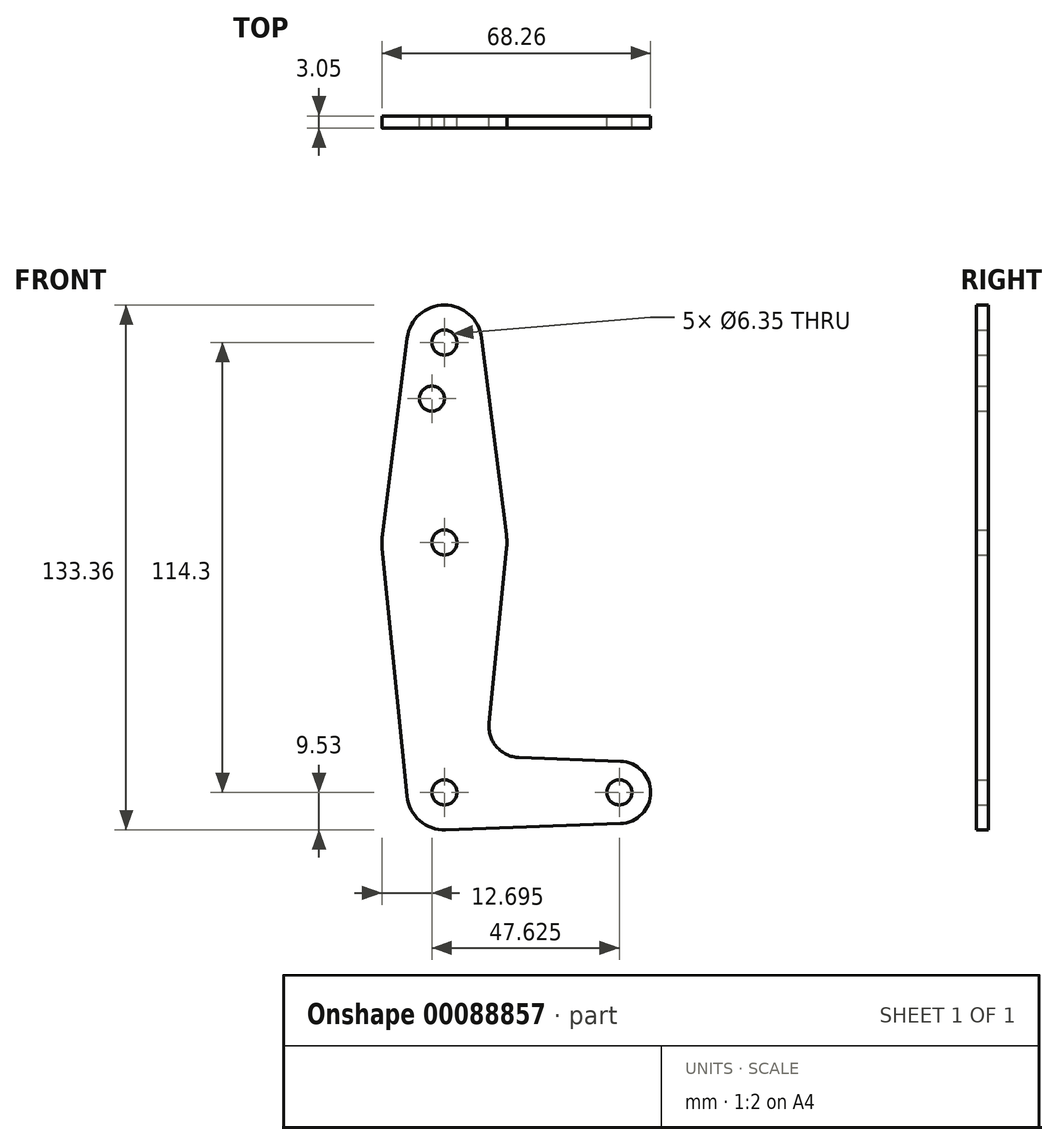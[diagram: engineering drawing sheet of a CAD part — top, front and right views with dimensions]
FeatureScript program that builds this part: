
annotation { "Feature Type Name" : "Feature", "Feature Type Description" : "" }
export const myFeature = defineFeature(function(context is Context, id is Id, definition is map)
    precondition{}
    {
        {
            var Q0;
            Q0=qCreatedBy(makeId("Front.planeOp"),FACE);
            var sketch = newSketch(context, id + "F0", { "sketchPlane" : qUnion([Q0])});
            skCircle(sketch, "E0", {"center": v(0, 114.3) * mm, "radius": 9.53 * mm});
            skCircle(sketch, "E1", {"center": v(0, 63.5) * mm, "radius": 15.88 * mm});
            skCircle(sketch, "E2", {"center": v(0, 0) * mm, "radius": 9.53 * mm});
            skCircle(sketch, "E3", {"center": v(44.45, 0) * mm, "radius": 7.94 * mm});
            skLineSegment(sketch, "E4", {"start": v(0, 0) * mm, "end": v(44.45, 0) * mm, "construction": true});
            skLineSegment(sketch, "E5", {"start": v(0, 114.3) * mm, "end": v(0, 0) * mm, "construction": true});
            skLineSegment(sketch, "E6", {"start": v(0.34, -9.52) * mm, "end": v(44.73, -7.93) * mm});
            skLineSegment(sketch, "E7", {"start": v(18.97, 8.85) * mm, "end": v(44.73, 7.93) * mm});
            skCircle(sketch, "E8", {"center": v(0, 114.3) * mm, "radius": 3.18 * mm});
            skLineSegment(sketch, "E9", {"start": v(-9.45, 115.5) * mm, "end": v(-15.75, 65.48) * mm});
            skLineSegment(sketch, "E10", {"start": v(-15.8, 61.91) * mm, "end": v(-9.48, -0.95) * mm});
            skLineSegment(sketch, "E11", {"start": v(9.45, 115.5) * mm, "end": v(15.75, 65.48) * mm});
            skLineSegment(sketch, "E12", {"start": v(15.8, 61.91) * mm, "end": v(11.34, 17.6) * mm});
            skCircle(sketch, "E13", {"center": v(0, 0) * mm, "radius": 3.18 * mm});
            skCircle(sketch, "E14", {"center": v(44.45, 0) * mm, "radius": 3.18 * mm});
            skCircle(sketch, "E15", {"center": v(0, 63.5) * mm, "radius": 3.18 * mm});
            skArc(sketch, "E16.filletArc", {"start": v(11.34, 17.6) * mm, "mid": v(13.26, 11.57) * mm, "end": v(18.97, 8.85) * mm});
            skCircle(sketch, "E17", {"center": v(-3.18, 100.03) * mm, "radius": 3.18 * mm});
            skSolve(sketch);
        }
        {
            var Q0;
            Q0 = qSketchRegion(id + "F0", true);
            extrude(context, id + "F1", {"entities" : qUnion([Q0]), "depth" : 3.05 * mm});
        }
    });
